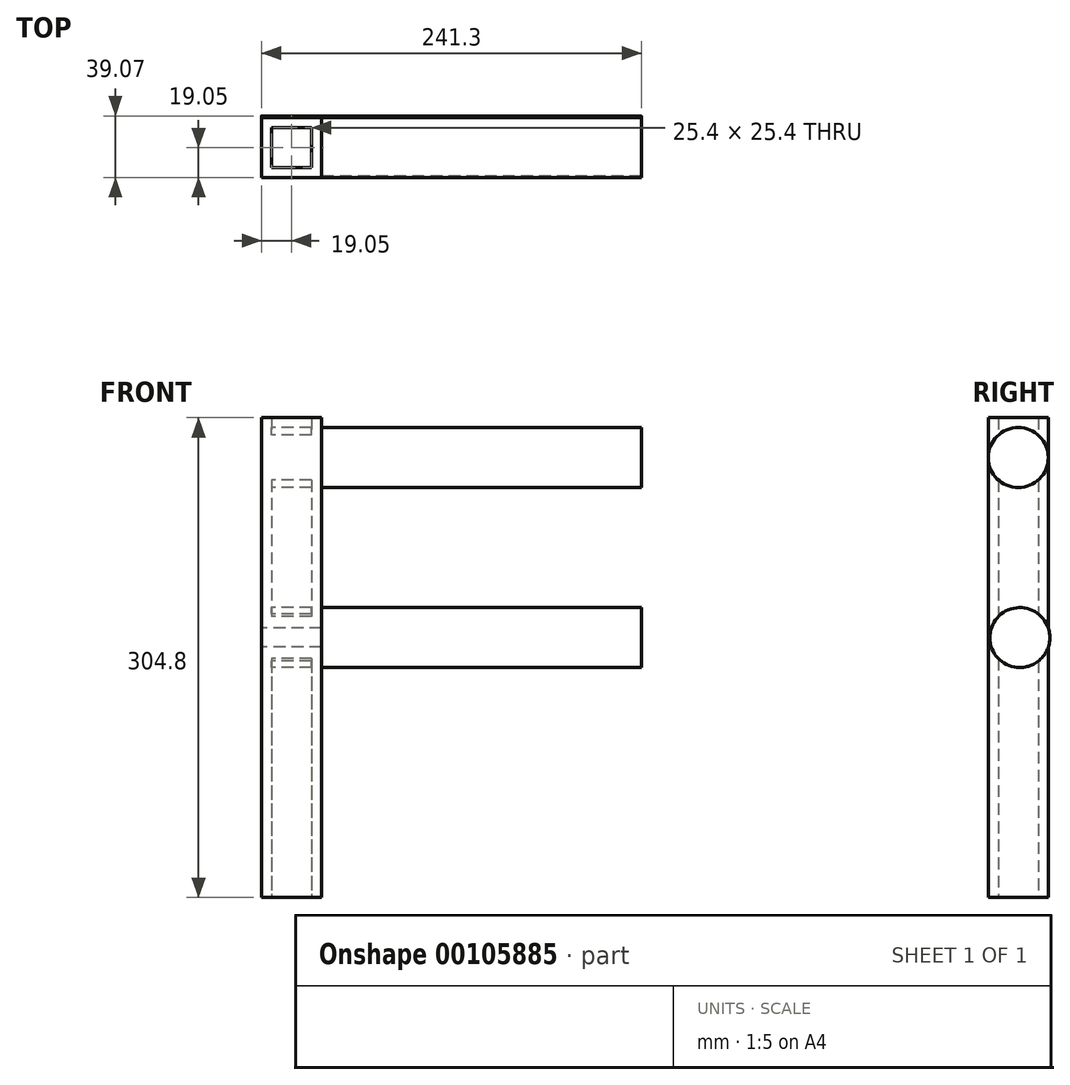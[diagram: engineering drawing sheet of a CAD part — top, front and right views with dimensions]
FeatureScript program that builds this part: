
annotation { "Feature Type Name" : "Feature", "Feature Type Description" : "" }
export const myFeature = defineFeature(function(context is Context, id is Id, definition is map)
    precondition{}
    {
        {
            var Q0;
            Q0=qCreatedBy(makeId("Top.planeOp"),FACE);
            var sketch = newSketch(context, id + "F0", { "sketchPlane" : qUnion([Q0])});
            skLineSegment(sketch, "E0.bottom", {"start": v(19.05, 19.05) * mm, "end": v(-19.05, 19.05) * mm});
            skLineSegment(sketch, "E0.top", {"start": v(19.05, -19.05) * mm, "end": v(-19.05, -19.05) * mm});
            skLineSegment(sketch, "E0.left", {"start": v(19.05, 19.05) * mm, "end": v(19.05, -19.05) * mm});
            skLineSegment(sketch, "E0.right", {"start": v(-19.05, 19.05) * mm, "end": v(-19.05, -19.05) * mm});
            skPoint(sketch, "E0.middle", {"position": v(0, 0) * mm});
            skLineSegment(sketch, "E1.0", {"start": v(12.7, 12.7) * mm, "end": v(-12.7, 12.7) * mm});
            skLineSegment(sketch, "E1.1", {"start": v(12.7, 12.7) * mm, "end": v(12.7, -12.7) * mm});
            skLineSegment(sketch, "E1.2", {"start": v(12.7, -12.7) * mm, "end": v(-12.7, -12.7) * mm});
            skLineSegment(sketch, "E1.3", {"start": v(-12.7, 12.7) * mm, "end": v(-12.7, -12.7) * mm});
            skSolve(sketch);
        }
        {
            var Q0;
            Q0=qSketchRegion(id+"F0",true);
            extrude(context, id + "F1", {"entities" : qUnion([Q0]), "depth" : 304.8 * mm});
        }
        {
            var Q0;
            Q0=makeQuery(id+"F1.opExtrude","SWEPT_FACE",FACE,{"disambiguationData":[OSD([sQuery(id+"F0.wireOp",EDGE,"E0.left")])]});
            var sketch = newSketch(context, id + "F2", { "sketchPlane" : qUnion([Q0])});
            skCircle(sketch, "E2", {"center": v(0, 279.4) * mm, "radius": 19.05 * mm});
            skCircle(sketch, "E3.1.0.0", {"center": v(0.97, 165.1) * mm, "radius": 19.05 * mm});
            skLineSegment(sketch, "E3.direction1", {"start": v(0, 279.4) * mm, "end": v(0.97, 165.1) * mm, "construction": true});
            skSolve(sketch);
        }
        {
            var Q0;
            Q0 = qSketchRegion(id + "F2", true);
            var Q1;
            Q1=makeQuery(id+"F1.opExtrude","SWEPT_FACE",FACE,{"disambiguationData":[OSD([sQuery(id+"F0.wireOp",EDGE,"E0.right")])]});
            extrude(context, id + "F3", {"entities" : qUnion([Q0]), "operationType" : NewBodyOperationType.ADD, "depth" : 203.2 * mm, "hasSecondDirection" : true, "secondDirectionBound" : SecondDirectionBoundingType.UP_TO_SURFACE, "secondDirectionOppositeDirection" : true, "secondDirectionBoundEntityFace" : qUnion([Q1]), "secondDirectionDepth" : 25.4 * mm});
        }
    });
